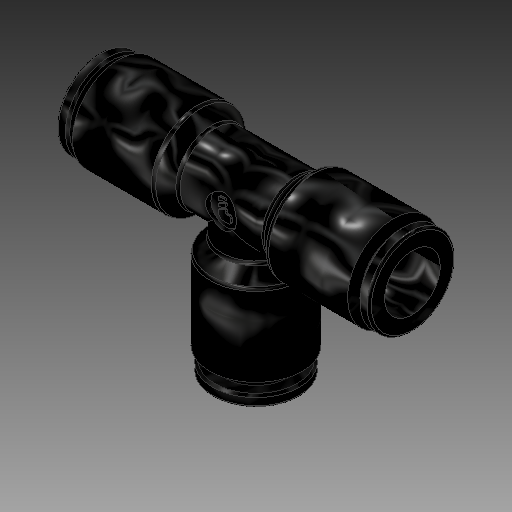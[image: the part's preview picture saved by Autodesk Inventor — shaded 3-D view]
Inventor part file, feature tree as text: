
AUTODESK INVENTOR PART (.ipt)
format: ipt  version: 2018 (Build 220112000, 112)  size: 324,608 bytes
history: native  units: in
note: dims shown in document units (in); Inventor stores cm internally (conversion verified against a paired STEP export)
features: extrude x2, sketch x2
ambient origin geometry x8: Origin, YZ Plane, XZ Plane, XY Plane, X Axis, Y Axis, Z Axis, Center Point
bodies: Solid1 (feature_tree)
feature tree (4):
  extrude  "Extrusion1"  Depth=1.0in TaperAngle=0.0deg
  extrude  "Extrusion2"  Depth=0.578in TaperAngle=0.0deg
  sketch  "Sketch1"  dims[d0=0.25in d1=1.0in d2=0.0in]
  sketch  "Sketch2"  dims[d3=0.25in d4=0.578in d5=0.0in]
